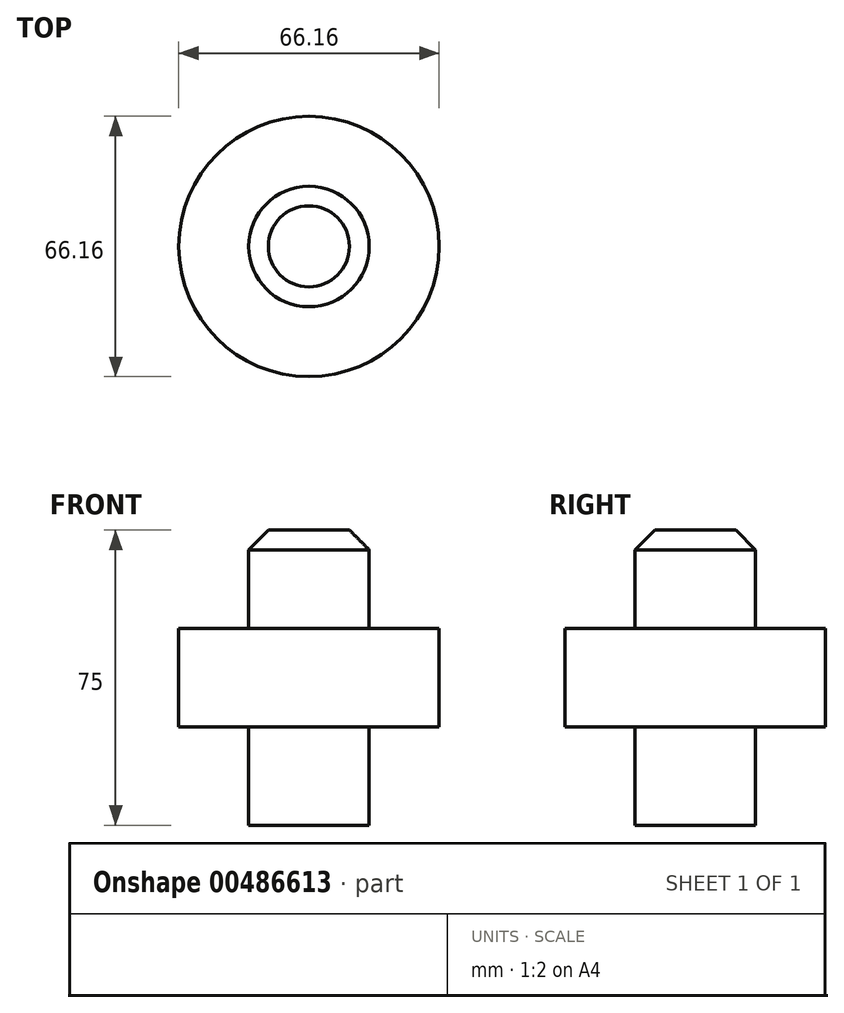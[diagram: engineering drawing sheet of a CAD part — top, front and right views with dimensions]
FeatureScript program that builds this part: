
annotation { "Feature Type Name" : "Feature", "Feature Type Description" : "" }
export const myFeature = defineFeature(function(context is Context, id is Id, definition is map)
    precondition{}
    {
        {
            var Q0;
            Q0=qCreatedBy(makeId("Top.planeOp"),FACE);
            var sketch = newSketch(context, id + "F0", { "sketchPlane" : qUnion([Q0])});
            skCircle(sketch, "E0", {"center": v(0, 0) * mm, "radius": 33.08 * mm});
            skSolve(sketch);
        }
        {
            var Q0;
            Q0=makeQuery(id+"F0.imprint","IMPRINT",FACE,{"disambiguationData":[TD([[makeQuery(id+"F0.imprint","IMPRINT",EDGE,{"derivedFrom":sQuery(id+"F0.wireOp",EDGE,"E0")}),1.0]])]});
            extrude(context, id + "F1", {"entities" : qUnion([Q0]), "depth" : 25 * mm});
        }
        {
            var Q0;
            Q0=makeQuery(id+"F1.opExtrude","CAP_FACE",FACE,{"disambiguationData":[OSD([sQuery(id+"F0.wireOp",EDGE,"E0")])],"isStart":false});
            var sketch = newSketch(context, id + "F2", { "sketchPlane" : qUnion([Q0])});
            skCircle(sketch, "E1", {"center": v(0, 0) * mm, "radius": 15.3 * mm});
            skSolve(sketch);
        }
        {
            var Q0;
            Q0=makeQuery(id+"F2.imprint","IMPRINT",FACE,{"disambiguationData":[TD([[makeQuery(id+"F2.imprint","IMPRINT",EDGE,{"derivedFrom":sQuery(id+"F2.wireOp",EDGE,"E1")}),1.0]])]});
            extrude(context, id + "F3", {"entities" : qUnion([Q0]), "operationType" : NewBodyOperationType.ADD, "depth" : 25 * mm});
        }
        {
            var Q0;
            Q0=makeQuery(id+"F3.opExtrude","CAP_EDGE",EDGE,{"disambiguationData":[OSD([sQuery(id+"F2.wireOp",EDGE,"E1")])],"isStart":false});
            chamfer(context, id + "F4", {"entities" : qUnion([Q0]), "width" : 5 * mm, "tangentPropagation" : true});
        }
        {
            var Q0;
            Q0=makeQuery(id+"F1.opExtrude","CAP_FACE",FACE,{"disambiguationData":[OSD([sQuery(id+"F0.wireOp",EDGE,"E0")])],"isStart":true});
            var sketch = newSketch(context, id + "F5", { "sketchPlane" : qUnion([Q0])});
            skCircle(sketch, "E2", {"center": v(0, 0) * mm, "radius": 15.3 * mm});
            skSolve(sketch);
        }
        {
            var Q0;
            Q0=makeQuery(id+"F5.imprint","IMPRINT",FACE,{"disambiguationData":[TD([[makeQuery(id+"F5.imprint","IMPRINT",EDGE,{"derivedFrom":sQuery(id+"F5.wireOp",EDGE,"E2")}),1.0]])]});
            extrude(context, id + "F6", {"entities" : qUnion([Q0]), "operationType" : NewBodyOperationType.ADD, "depth" : 25 * mm});
        }
        {
            var Q0;
            Q0=qCreatedBy(makeId("Front.planeOp"),FACE);
            cPlane(context, id + "F7", {"entities" : qUnion([Q0]), "cplaneType" : CPlaneType.OFFSET, "offset" : 25 * mm, "width" : 150 * mm, "height" : 150 * mm});
        }
    });
